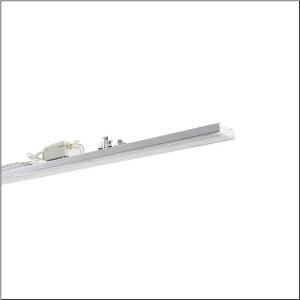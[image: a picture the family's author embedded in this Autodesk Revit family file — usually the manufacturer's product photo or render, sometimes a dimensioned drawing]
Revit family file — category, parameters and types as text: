
# Revit family: licross_21_recessed_mo_52te12dv4fxg3s
name_source: partatom
category: Lighting Fixtures
units: mm (PartAtom-declared; Revit-internal decimal feet)

## family parameters
Cut with Voids When Loaded = No
Host = Face
Light Source = No
Part Type = Normal
Room Calculation Point = No
Round Connector Dimension = Use Diameter
Shared = No

## types (1)
- --- (1 x LED, 950 lm, 5.5 W, 4000K)
    Apparent Load = 6 VA
    CIE Flux Codes = 72 92 99 100 100
    Color Rendering = 80
    Color Temperature = 4000K
    Default Elevation = 1800 mm
    Description = Licross 21 Recessed MO, luminaire insert, of sheet steel, galvanised, coil coated, white, length: 2.250mm, width: 66mm, height: 67mm, LED rated luminous flux: 15.420lm, light colour: 840, SDCM (Standard Deviation of Colour Matching)MacAdam ≤ 3 SDCM (initial), control gear: DALI 2 (for two DALI lines), with plug, 6-pole, with phase selection, for trunking rail, 14-core, mains connection: 220..240V, AC, 50/60Hz, rated input power: 89W, for trunking rail, 14-core, internal wiring halogen-free, for emergency light function, converter,control gear: single battery element, battery: LiFePO4, 9Ah, primary optical cover: cover, of PMMA, light emission: direct distribution, primary light characteristic: symmetric, protection rating (complete): IP54, insulation class (complete): insulation class I (protective earthing), certification: CE, UKCA, protection symbol: D if used in an environment with non-conductive dust loads with corresponding accessories, impact resistance: IK06, permissible ambient temperature for indoor applications: +5..+35°C, standard: EN 60598-2-22, LABS conformity tested according to VDMA 24364:2018-05, reducing of maximum allowable ambient temperature of 5°C with ceiling mounting, corresponds to IFS (International Featured Standards) requirements for safety and quality in the food industry, The light source and the operating device comply with the requirements of the Ecodesign Regulation (EU) 2019/2020 and are replaceable in accordance with this regulation, packaging unit: 1 piece
    Height = 58 mm
    Lamp = 1 x LED
    Lamp Light Flux = 950 lm
    Lamp Power = 5.5 W
    Lamp count = 1
    Length = 2250 mm
    Luminous efficacy = 173 lm/W
    Manufacturer = Siteco
    ModVariant = No
    Model = 52TE12DV4FXG3S
    Mounting Place = Ceiling
    Mounting Type = Pendant
    Number of Poles = 1
    OnlyDefault = Yes
    Power Factor = 1
    Product Name = Licross 21 Recessed MO
    Product group = luminaire insert | ceiling pendant
    ProductGroupID = 901
    Protection Class = Protection class I
    Protection Degree = IP 54
    RLX_Detail_Level = 1
    RLX_Emergency_Light_Flux = 0 lm
    RLX_Emergency_Type = 0
    RLX_Emergency_Type_DB = No
    RlxData = <blob elided: 30289 chars, md5=a4c2524a>
    Socket = socket
    Standby Power = 0 W
    System Light Flux = 950 lm
    System Power = 6 W
    Type Comments = : emergency light operation: 3 h
    Type Image = l_1296930.jpg
    URL = http://relux.com
    VarID = @adj_111573
    Voltage = 0 V
    Weight = 0.00 kg
    Width = 66 mm

## geometry (parser evidence)
native form markers: Blend x4, Sweep x10
no freeform markers — native parametric forms only
